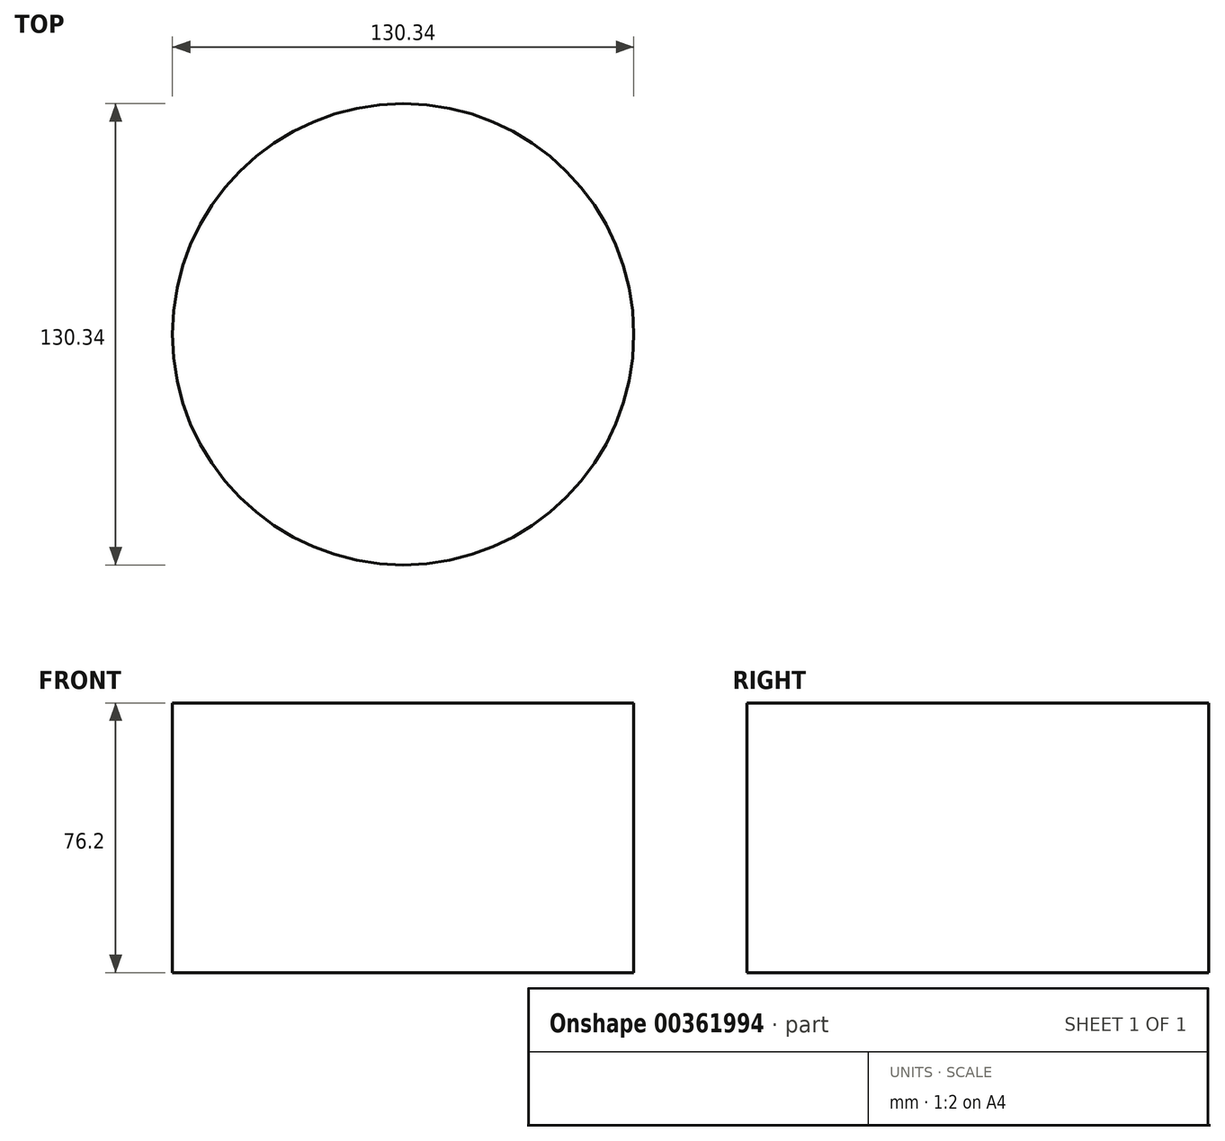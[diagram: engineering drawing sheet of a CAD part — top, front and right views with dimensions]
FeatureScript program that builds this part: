
annotation { "Feature Type Name" : "Feature", "Feature Type Description" : "" }
export const myFeature = defineFeature(function(context is Context, id is Id, definition is map)
    precondition{}
    {
        {
            var Q0;
            Q0=qCreatedBy(makeId("Top.planeOp"),FACE);
            var sketch = newSketch(context, id + "F0", { "sketchPlane" : qUnion([Q0])});
            skCircle(sketch, "E0", {"center": v(0, 0) * mm, "radius": 75.72 * mm});
            skCircle(sketch, "E1", {"center": v(0, 0) * mm, "radius": 65.17 * mm});
            skSolve(sketch);
        }
        {
            var Q0;
            Q0=makeQuery(id+"F0.imprint","IMPRINT",FACE,{"disambiguationData":[TD([[makeQuery(id+"F0.imprint","IMPRINT",EDGE,{"derivedFrom":sQuery(id+"F0.wireOp",EDGE,"E1")}),1.0]])]});
            extrude(context, id + "F1", {"entities" : qUnion([Q0]), "depth" : 76.2 * mm});
        }
    });
